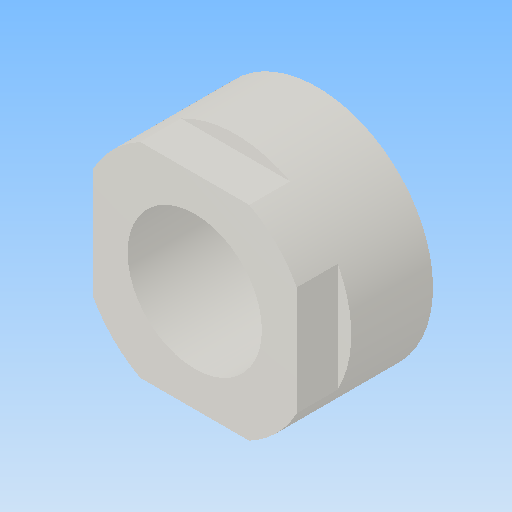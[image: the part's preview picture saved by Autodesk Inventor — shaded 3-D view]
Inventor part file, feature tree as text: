
AUTODESK INVENTOR PART (.ipt)
format: ipt  version: 2018 (Build 220112000, 112)  size: 112,128 bytes
history: native  units: mm
features: extrude x2, sketch x2
ambient origin geometry x8: Origin, YZ Plane, XZ Plane, XY Plane, X Axis, Y Axis, Z Axis, Center Point
bodies: Solid1 (feature_tree)
feature tree (4):
  extrude  "Extrusion1"  Depth=17.0mm
  extrude  "Extrusion2"  Depth=15.0mm
  sketch  "Sketch1"  dims[d0=9.8602mm d1=17.0mm]
  sketch  "Sketch2"  dims[d2=9.0mm d3=0.0mm d4=15.0mm d5=3.0mm d6=0.0mm]
